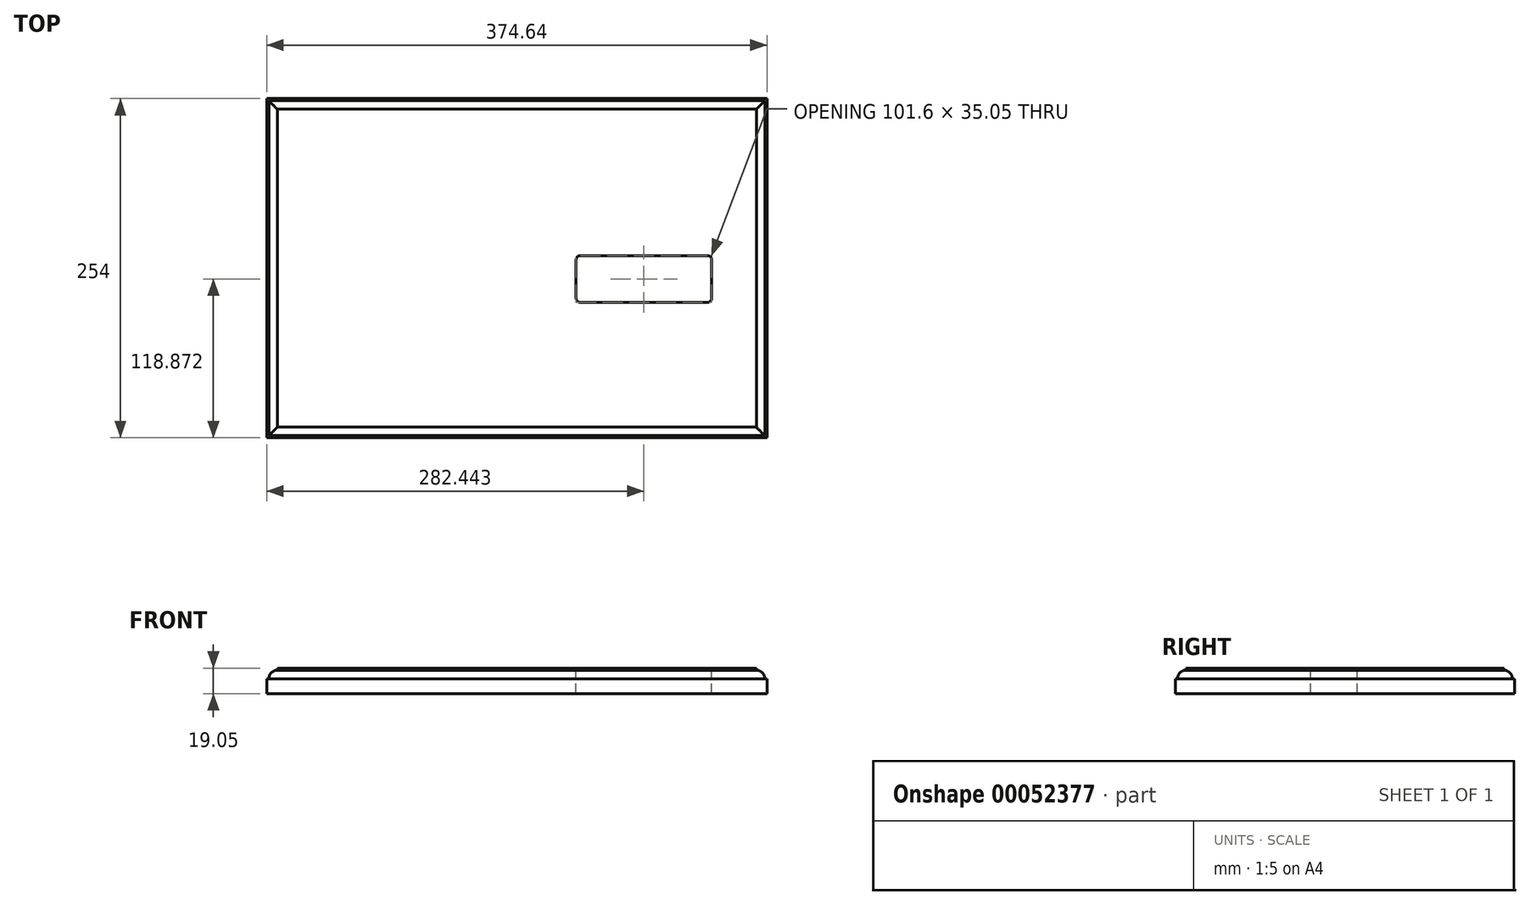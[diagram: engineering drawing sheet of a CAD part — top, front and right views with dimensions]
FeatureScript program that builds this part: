
annotation { "Feature Type Name" : "Feature", "Feature Type Description" : "" }
export const myFeature = defineFeature(function(context is Context, id is Id, definition is map)
    precondition{}
    {
        {
            var Q0;
            Q0=qCreatedBy(makeId("Top.planeOp"),FACE);
            var sketch = newSketch(context, id + "F0", { "sketchPlane" : qUnion([Q0])});
            skLineSegment(sketch, "E0.rect.bottom", {"start": v(187.33, -127) * mm, "end": v(-187.33, -127) * mm});
            skLineSegment(sketch, "E0.rect.top", {"start": v(187.33, 127) * mm, "end": v(-187.33, 127) * mm});
            skLineSegment(sketch, "E0.rect.left", {"start": v(187.33, -127) * mm, "end": v(187.33, 127) * mm});
            skLineSegment(sketch, "E0.rect.right", {"start": v(-187.33, -127) * mm, "end": v(-187.33, 127) * mm});
            skPoint(sketch, "E0.rect.middle", {"position": v(0, 0) * mm});
            skLineSegment(sketch, "E1.rect.bottom", {"start": v(142.75, 9.4) * mm, "end": v(47.5, 9.4) * mm});
            skLineSegment(sketch, "E1.rect.top", {"start": v(142.75, -25.65) * mm, "end": v(47.5, -25.65) * mm});
            skLineSegment(sketch, "E1.rect.left", {"start": v(145.92, 6.22) * mm, "end": v(145.92, -22.48) * mm});
            skLineSegment(sketch, "E1.rect.right", {"start": v(44.32, 6.22) * mm, "end": v(44.32, -22.48) * mm});
            skPoint(sketch, "E1.rect.middle", {"position": v(95.12, -8.13) * mm});
            skPoint(sketch, "E2.visualSharp", {"position": v(44.32, 9.4) * mm});
            skArc(sketch, "E2.filletArc", {"start": v(47.5, 9.4) * mm, "mid": v(45.25, 8.47) * mm, "end": v(44.32, 6.22) * mm});
            skPoint(sketch, "E3.visualSharp", {"position": v(145.92, 9.4) * mm});
            skArc(sketch, "E3.filletArc", {"start": v(145.92, 6.22) * mm, "mid": v(145, 8.47) * mm, "end": v(142.75, 9.4) * mm});
            skPoint(sketch, "E4.visualSharp", {"position": v(145.92, -25.65) * mm});
            skArc(sketch, "E4.filletArc", {"start": v(142.75, -25.65) * mm, "mid": v(145, -24.72) * mm, "end": v(145.92, -22.48) * mm});
            skPoint(sketch, "E5.visualSharp", {"position": v(44.32, -25.65) * mm});
            skArc(sketch, "E5.filletArc", {"start": v(44.32, -22.48) * mm, "mid": v(45.25, -24.72) * mm, "end": v(47.5, -25.65) * mm});
            skSolve(sketch);
        }
        {
            var Q0;
            Q0 = qSketchRegion(id + "F0", true);
            extrude(context, id + "F1", {"entities" : qUnion([Q0]), "oppositeDirection" : true, "depth" : 19.05 * mm});
        }
        {
            var Q0;
            Q0=qCreatedBy(makeId("Front.planeOp"),FACE);
            var sketch = newSketch(context, id + "F2", { "sketchPlane" : qUnion([Q0])});
            skLineSegment(sketch, "E6", {"start": v(179.37, 0) * mm, "end": v(179.37, -1.6) * mm});
            skLineSegment(sketch, "E7", {"start": v(187.33, -7.95) * mm, "end": v(185.72, -7.95) * mm});
            skArc(sketch, "E8", {"start": v(185.72, -7.95) * mm, "mid": v(183.86, -3.46) * mm, "end": v(179.37, -1.6) * mm});
            skLineSegment(sketch, "E9", {"start": v(179.37, 0) * mm, "end": v(187.33, 0) * mm});
            skLineSegment(sketch, "E10", {"start": v(187.33, 0) * mm, "end": v(187.33, -7.95) * mm});
            skLineSegment(sketch, "E11.MirrorCS", {"start": v(-179.37, 0) * mm, "end": v(-179.37, -1.6) * mm});
            skLineSegment(sketch, "E12.MirrorCS", {"start": v(-187.33, -7.95) * mm, "end": v(-185.72, -7.95) * mm});
            skArc(sketch, "E13.MirrorCS", {"start": v(-185.72, -7.95) * mm, "mid": v(-183.86, -3.46) * mm, "end": v(-179.37, -1.6) * mm});
            skLineSegment(sketch, "E14.MirrorCS", {"start": v(-179.37, 0) * mm, "end": v(-187.33, 0) * mm});
            skLineSegment(sketch, "E15.MirrorCS", {"start": v(-187.33, 0) * mm, "end": v(-187.33, -7.95) * mm});
            skSolve(sketch);
        }
        {
            var Q0;
            Q0 = qSketchRegion(id + "F2", true);
            extrude(context, id + "F3", {"entities" : qUnion([Q0]), "operationType" : NewBodyOperationType.REMOVE, "oppositeDirection" : true, "depth" : 304.8 * mm, "symmetric" : true});
        }
        {
            var Q0;
            Q0=qCreatedBy(makeId("Right.planeOp"),FACE);
            var sketch = newSketch(context, id + "F4", { "sketchPlane" : qUnion([Q0])});
            skLineSegment(sketch, "E16", {"start": v(119.05, 0) * mm, "end": v(119.05, -1.6) * mm});
            skLineSegment(sketch, "E17", {"start": v(127, -7.95) * mm, "end": v(125.4, -7.95) * mm});
            skArc(sketch, "E18", {"start": v(125.4, -7.95) * mm, "mid": v(123.54, -3.46) * mm, "end": v(119.05, -1.6) * mm});
            skLineSegment(sketch, "E19", {"start": v(119.05, 0) * mm, "end": v(127, 0) * mm});
            skLineSegment(sketch, "E20", {"start": v(127, 0) * mm, "end": v(127, -7.95) * mm});
            skLineSegment(sketch, "E21.MirrorCS", {"start": v(-119.05, 0) * mm, "end": v(-119.05, -1.6) * mm});
            skArc(sketch, "E22.MirrorCS", {"start": v(-125.4, -7.95) * mm, "mid": v(-123.54, -3.46) * mm, "end": v(-119.05, -1.6) * mm});
            skLineSegment(sketch, "E23.MirrorCS", {"start": v(-127, -7.95) * mm, "end": v(-125.4, -7.95) * mm});
            skLineSegment(sketch, "E24.MirrorCS", {"start": v(-119.05, 0) * mm, "end": v(-127, 0) * mm});
            skLineSegment(sketch, "E25.MirrorCS", {"start": v(-127, 0) * mm, "end": v(-127, -7.95) * mm});
            skSolve(sketch);
        }
        {
            var Q0;
            Q0 = qSketchRegion(id + "F4", true);
            extrude(context, id + "F5", {"entities" : qUnion([Q0]), "operationType" : NewBodyOperationType.REMOVE, "oppositeDirection" : true, "depth" : 406.4 * mm, "symmetric" : true});
        }
    });
